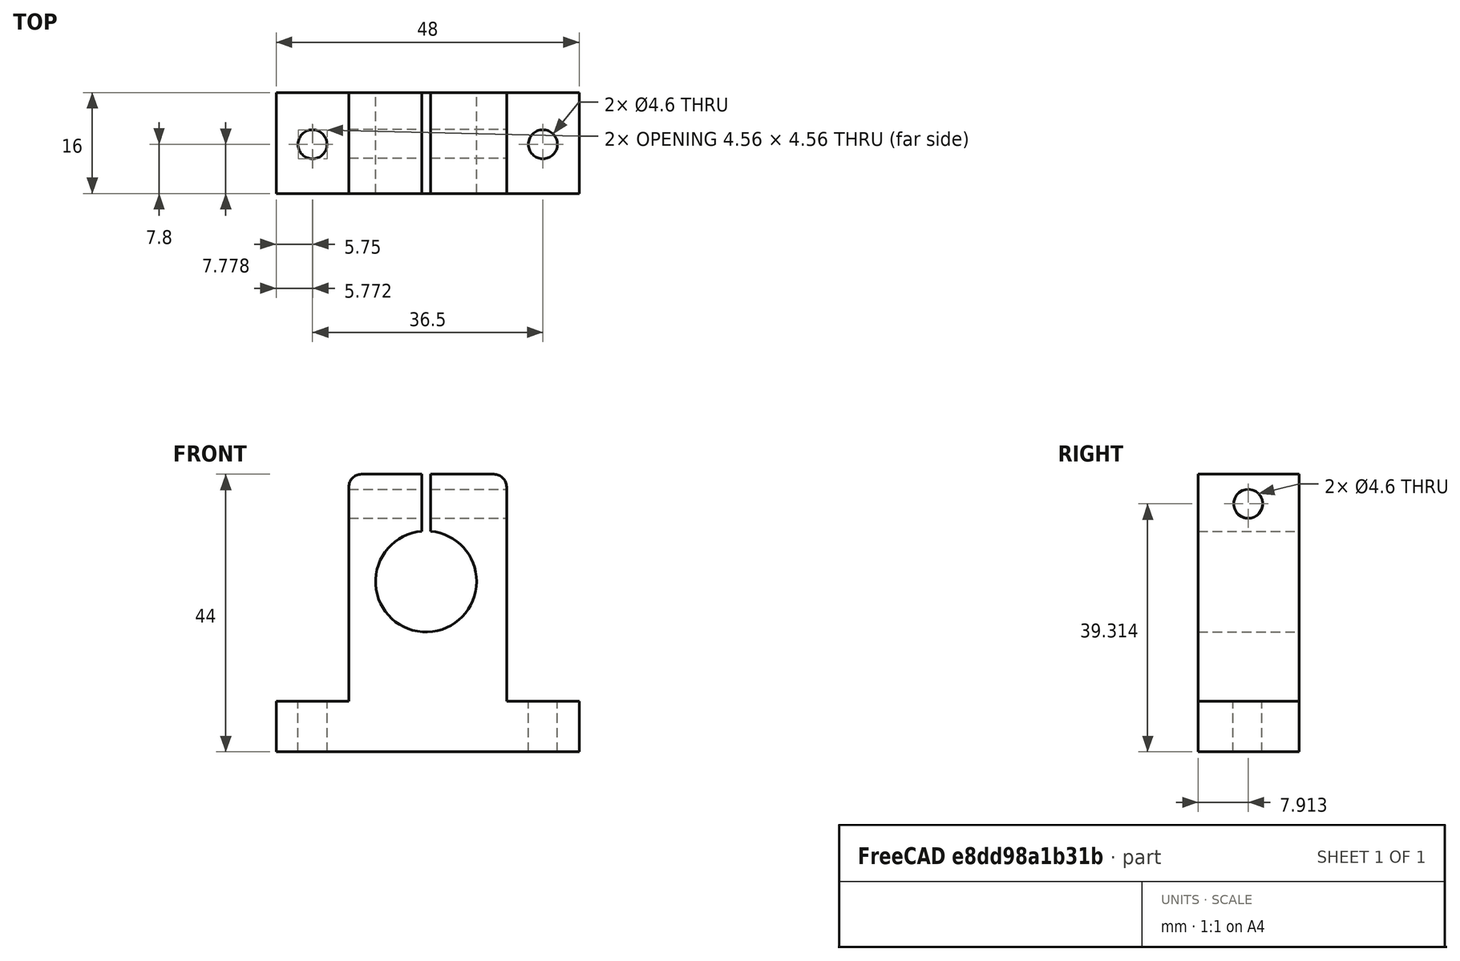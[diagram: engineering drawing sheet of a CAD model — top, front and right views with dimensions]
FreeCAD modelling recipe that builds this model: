
FCSTD DOCUMENT
Label: sk16
objects: Part::Cut×5, Part::Cylinder×4, Part::Box×3, Part::Fillet×2, Part::MultiFuse×1
note: 15 computed .brp shape members not serialized (recipe doc carries the construction recipe); baked Part::Feature solids carry a one-line shape summary decoded from their .brp

FEATURE [Part::Box] Box
  Height = 8
  Length = 48
  Width = 16
FEATURE [Part::Box] Box001
  Height = 36
  Length = 25
  Placement = pos=(11.5,0,8) rot=(0,0,1;0rad)
  Width = 16
FEATURE [Part::Cylinder] Cylinder
  Angle = 360
  Height = 30
  Placement = pos=(23.7403,-8.80917,27) rot=(-1,0,0;1.5708rad)
  Radius = 8
FEATURE [Part::MultiFuse] Fusion
  Shapes = -> [Box,Box001]
FEATURE [Part::Cut] Cut
  Base = -> Fusion
  Tool = -> Cylinder
FEATURE [Part::Box] Box002
  Height = 20
  Length = 1.4
  Placement = pos=(23.0742,-2.91866,34.284) rot=(0,0,1;0rad)
  Width = 20
FEATURE [Part::Cut] Cut001
  Base = -> Cut
  Tool = -> Box002
FEATURE [Part::Cylinder] Cylinder001
  Angle = 360
  Height = 10
  Placement = pos=(5.75,7.8,-0.597231) rot=(0,0,1;0rad)
  Radius = 2.3
FEATURE [Part::Cylinder] Cylinder002
  Angle = 360
  Height = 10
  Placement = pos=(42.25,7.8,-0.597231) rot=(0,0,1;0rad)
  Radius = 2.3
FEATURE [Part::Cut] Cut002
  Base = -> Cut001
  Tool = -> Cylinder001
FEATURE [Part::Cut] Cut003
  Base = -> Cut002
  Tool = -> Cylinder002
FEATURE [Part::Cylinder] Cylinder003
  Angle = 360
  Height = 40
  Placement = pos=(3.68756,7.91256,39.3136) rot=(0,1,0;1.5708rad)
  Radius = 2.3
FEATURE [Part::Cut] Cut004
  Base = -> Cut003
  Tool = -> Cylinder003
FEATURE [Part::Fillet] Fillet
  Base = -> Cut004
  Edges = 1 edges r=2: [Edge50]
FEATURE [Part::Fillet] Fillet001
  Base = -> Fillet
  Edges = 1 edges r=2: [Edge27]
